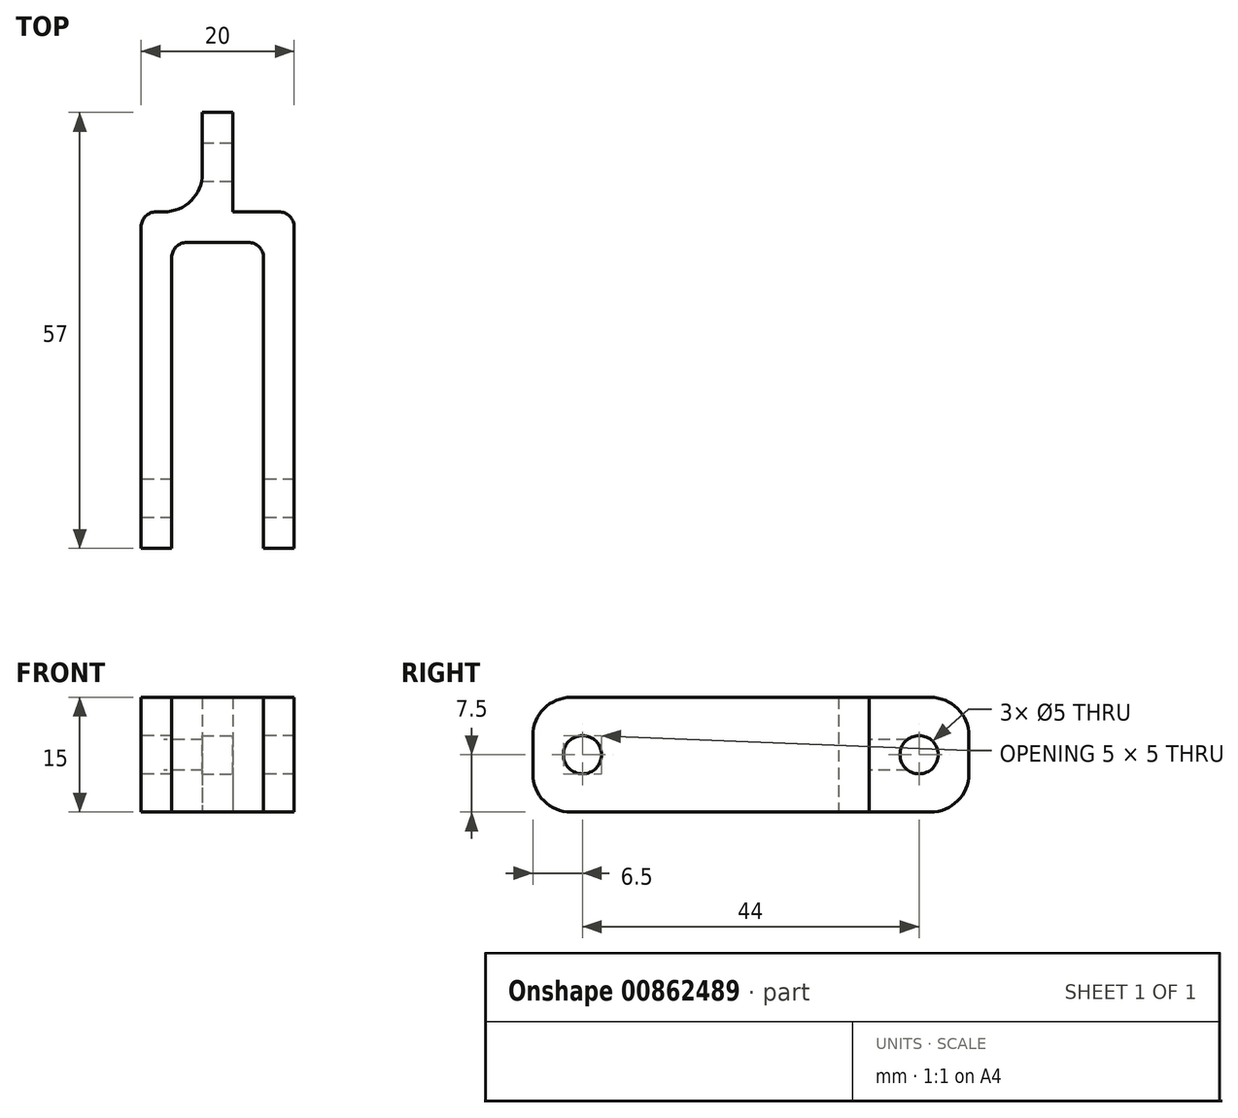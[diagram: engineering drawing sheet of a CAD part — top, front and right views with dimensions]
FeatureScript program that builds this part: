
annotation { "Feature Type Name" : "Feature", "Feature Type Description" : "" }
export const myFeature = defineFeature(function(context is Context, id is Id, definition is map)
    precondition{}
    {
        {
            var Q0;
            Q0=qCreatedBy(makeId("Top.planeOp"),FACE);
            var sketch = newSketch(context, id + "F0", { "sketchPlane" : qUnion([Q0])});
            skLineSegment(sketch, "E0", {"start": v(0, 44) * mm, "end": v(20, 44) * mm});
            skLineSegment(sketch, "E1", {"start": v(20, 44) * mm, "end": v(20, 0) * mm});
            skLineSegment(sketch, "E2", {"start": v(20, 0) * mm, "end": v(16, 0) * mm});
            skLineSegment(sketch, "E3", {"start": v(16, 0) * mm, "end": v(16, 40) * mm});
            skLineSegment(sketch, "E4", {"start": v(16, 40) * mm, "end": v(4, 40) * mm});
            skLineSegment(sketch, "E5", {"start": v(4, 40) * mm, "end": v(4, 0) * mm});
            skLineSegment(sketch, "E6", {"start": v(4, 0) * mm, "end": v(0, 0) * mm});
            skPoint(sketch, "E7.end.orphan", {"position": v(0, 3.7) * mm});
            skLineSegment(sketch, "E8", {"start": v(0, 44) * mm, "end": v(0, 0) * mm});
            skSolve(sketch);
        }
        {
            var Q0;
            Q0=makeQuery(id+"F0.imprint","IMPRINT",FACE,{"disambiguationData":[TD([[makeQuery(id+"F0.imprint","IMPRINT",EDGE,{"derivedFrom":sQuery(id+"F0.wireOp",EDGE,"E0")}),-1.0]])]});
            extrude(context, id + "F1", {"entities" : qUnion([Q0]), "depth" : 15 * mm, "offsetDistance" : 25 * mm});
        }
        {
            var Q0;
            Q0=makeQuery(id+"F1.opExtrude","SWEPT_FACE",FACE,{"disambiguationData":[OSD([sQuery(id+"F0.wireOp",EDGE,"E8")])]});
            var sketch = newSketch(context, id + "F2", { "sketchPlane" : qUnion([Q0])});
            skLineSegment(sketch, "E9", {"start": v(0, 7.5) * mm, "end": v(-14.8, 7.5) * mm, "construction": true});
            skLineSegment(sketch, "E10", {"start": v(-6.5, 0) * mm, "end": v(-6.5, 15) * mm, "construction": true});
            skCircle(sketch, "E11", {"center": v(-6.5, 7.5) * mm, "radius": 2.5 * mm});
            skSolve(sketch);
        }
        {
            var Q0;
            Q0=makeQuery(id+"F2.imprint","IMPRINT",FACE,{"disambiguationData":[TD([[makeQuery(id+"F2.imprint","IMPRINT",EDGE,{"derivedFrom":sQuery(id+"F2.wireOp",EDGE,"E11")}),1.0]])]});
            extrude(context, id + "F3", {"entities" : qUnion([Q0]), "operationType" : NewBodyOperationType.REMOVE, "oppositeDirection" : true, "depth" : 25 * mm, "offsetDistance" : 25 * mm});
        }
        {
            var Q0;
            Q0=makeQuery(id+"F1.opExtrude","SWEPT_FACE",FACE,{"disambiguationData":[OSD([sQuery(id+"F0.wireOp",EDGE,"E0")])]});
            var sketch = newSketch(context, id + "F4", { "sketchPlane" : qUnion([Q0])});
            skLineSegment(sketch, "E12", {"start": v(-10, 0) * mm, "end": v(-10, 15) * mm, "construction": true});
            skLineSegment(sketch, "E13", {"start": v(0, 7.5) * mm, "end": v(-20, 7.5) * mm, "construction": true});
            skLineSegment(sketch, "E14.bottom", {"start": v(-12, 15) * mm, "end": v(-8, 15) * mm});
            skLineSegment(sketch, "E14.top", {"start": v(-12, 0) * mm, "end": v(-8, 0) * mm});
            skLineSegment(sketch, "E14.left", {"start": v(-12, 15) * mm, "end": v(-12, 0) * mm});
            skLineSegment(sketch, "E14.right", {"start": v(-8, 15) * mm, "end": v(-8, 0) * mm});
            skPoint(sketch, "E14.middle", {"position": v(-10, 7.5) * mm});
            skSolve(sketch);
        }
        {
            var Q0;
            Q0=makeQuery(id+"F4.imprint","IMPRINT",FACE,{"disambiguationData":[TD([[makeQuery(id+"F4.imprint","IMPRINT",EDGE,{"derivedFrom":sQuery(id+"F4.wireOp",EDGE,"E14.bottom")}),1.0]])]});
            extrude(context, id + "F5", {"entities" : qUnion([Q0]), "operationType" : NewBodyOperationType.ADD, "depth" : 13 * mm, "offsetDistance" : 25 * mm});
        }
        {
            var Q0;
            Q0=makeQuery(id+"F5.opExtrude","SWEPT_FACE",FACE,{"disambiguationData":[OSD([sQuery(id+"F4.wireOp",EDGE,"E14.left")])]});
            var sketch = newSketch(context, id + "F6", { "sketchPlane" : qUnion([Q0])});
            skCircle(sketch, "E15", {"center": v(50.5, 7.5) * mm, "radius": 2.5 * mm});
            skPoint(sketch, "E15.centerSnap0", {"position": v(50.5, 15) * mm});
            skPoint(sketch, "E15.centerSnap1", {"position": v(57, 7.5) * mm});
            skSolve(sketch);
        }
        {
            var Q0;
            Q0=makeQuery(id+"F6.imprint","IMPRINT",FACE,{"disambiguationData":[TD([[makeQuery(id+"F6.imprint","IMPRINT",EDGE,{"derivedFrom":sQuery(id+"F6.wireOp",EDGE,"E15")}),1.0]])]});
            extrude(context, id + "F7", {"entities" : qUnion([Q0]), "operationType" : NewBodyOperationType.REMOVE, "oppositeDirection" : true, "depth" : 4 * mm, "offsetDistance" : 25 * mm});
        }
        {
            var Q0;
            Q0=makeQuery(id+"F5.opExtrude","CAP_EDGE",EDGE,{"disambiguationData":[OSD([sQuery(id+"F4.wireOp",EDGE,"E14.top")])],"isStart":false});
            var Q1;
            Q1=makeQuery(id+"F5.opExtrude","CAP_EDGE",EDGE,{"disambiguationData":[OSD([sQuery(id+"F4.wireOp",EDGE,"E14.bottom")])],"isStart":false});
            var Q2;
            Q2=makeQuery(id+"F1.opExtrude","CAP_EDGE",EDGE,{"disambiguationData":[OSD([sQuery(id+"F0.wireOp",EDGE,"E6")])],"isStart":false});
            var Q3;
            Q3=makeQuery(id+"F1.opExtrude","CAP_EDGE",EDGE,{"disambiguationData":[OSD([sQuery(id+"F0.wireOp",EDGE,"E2")])],"isStart":false});
            var Q4;
            Q4=makeQuery(id+"F1.opExtrude","CAP_EDGE",EDGE,{"disambiguationData":[OSD([sQuery(id+"F0.wireOp",EDGE,"E6")])],"isStart":true});
            var Q5;
            Q5=makeQuery(id+"F1.opExtrude","CAP_EDGE",EDGE,{"disambiguationData":[OSD([sQuery(id+"F0.wireOp",EDGE,"E2")])],"isStart":true});
            var Q6;
            Q6=makeQuery(id+"F5.opExtrude","CAP_EDGE",EDGE,{"disambiguationData":[OSD([sQuery(id+"F4.wireOp",EDGE,"E14.left")])],"isStart":true});
            var Q7;
            Q7=makeQuery(id+"F5.opExtrude","CAP_EDGE",EDGE,{"disambiguationData":[OSD([sQuery(id+"F4.wireOp",EDGE,"E14.right")])],"isStart":true});
            fillet(context, id + "F8", {"entities" : qUnion([Q0, Q1, Q2, Q3, Q4, Q5, Q6, Q7]), "radius" : 5 * mm, "tangentPropagation" : true, "allowEdgeOverflow" : false});
        }
        {
            var Q0;
            Q0=makeQuery(id+"F1.opExtrude","SWEPT_EDGE",EDGE,{"disambiguationData":[OSD([sQuery(id+"F0.wireOp",EDGE,"E3"),sQuery(id+"F0.wireOp",EDGE,"E4")])]});
            var Q1;
            Q1=makeQuery(id+"F1.opExtrude","SWEPT_EDGE",EDGE,{"disambiguationData":[OSD([sQuery(id+"F0.wireOp",EDGE,"E4"),sQuery(id+"F0.wireOp",EDGE,"E5")])]});
            var Q2;
            Q2=makeQuery(id+"F1.opExtrude","SWEPT_EDGE",EDGE,{"disambiguationData":[OSD([sQuery(id+"F0.wireOp",EDGE,"E0"),sQuery(id+"F0.wireOp",EDGE,"E1")])]});
            var Q3;
            Q3=makeQuery(id+"F1.opExtrude","SWEPT_EDGE",EDGE,{"disambiguationData":[OSD([sQuery(id+"F0.wireOp",EDGE,"E0"),sQuery(id+"F0.wireOp",EDGE,"E8")])]});
            fillet(context, id + "F9", {"entities" : qUnion([Q0, Q1, Q2, Q3]), "radius" : 2 * mm, "tangentPropagation" : true, "allowEdgeOverflow" : false});
        }
    });
